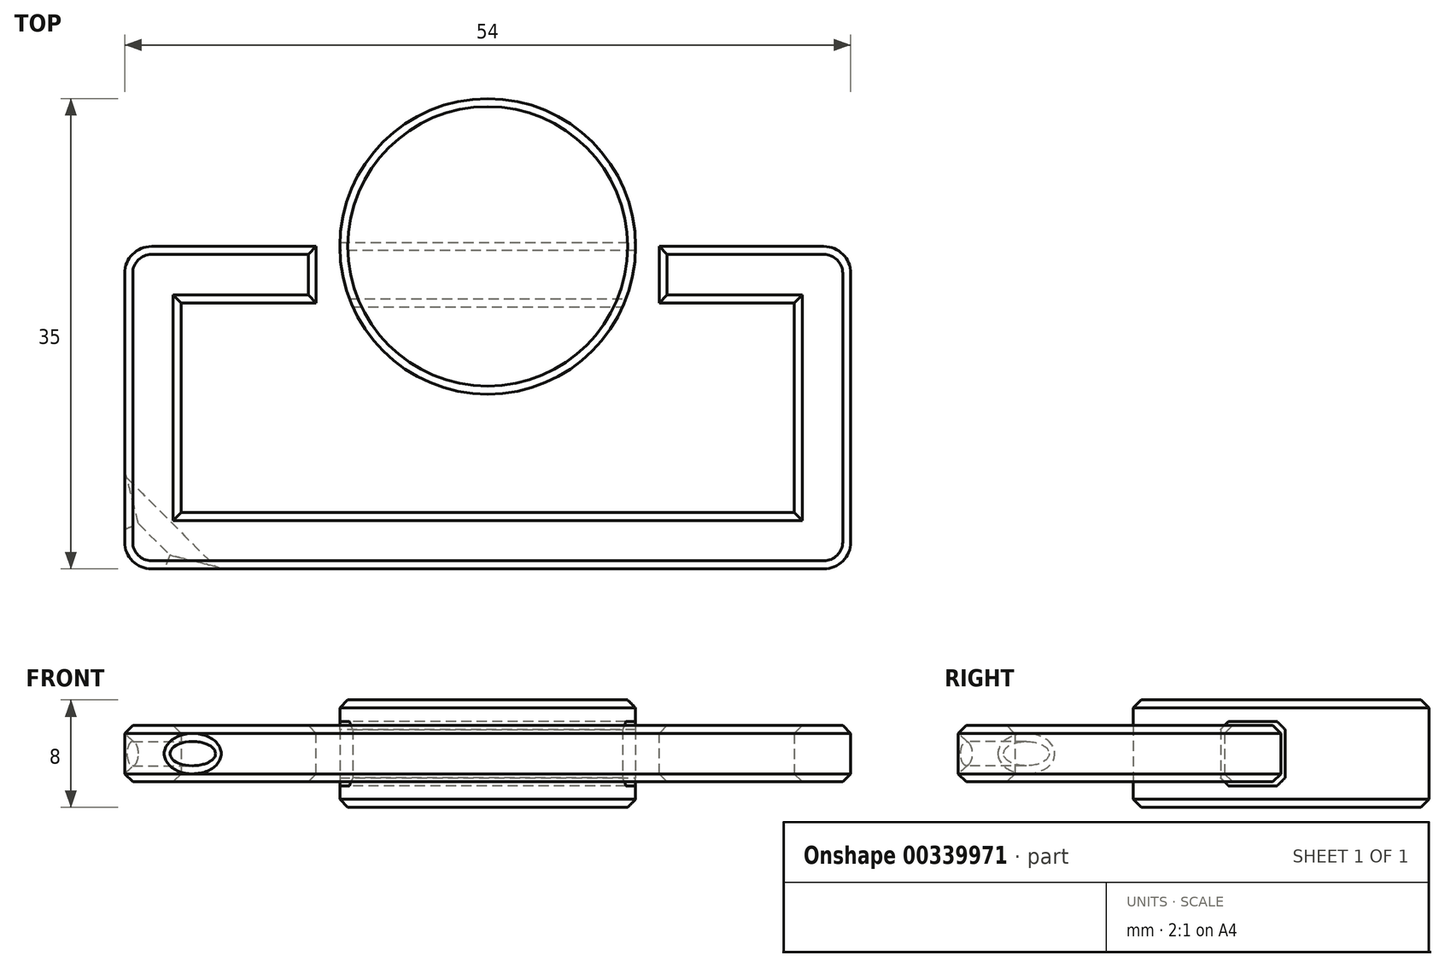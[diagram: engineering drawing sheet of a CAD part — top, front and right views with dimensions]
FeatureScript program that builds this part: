
annotation { "Feature Type Name" : "Feature", "Feature Type Description" : "" }
export const myFeature = defineFeature(function(context is Context, id is Id, definition is map)
    precondition{}
    {
        {
            var Q0;
            Q0=qCreatedBy(makeId("Top.planeOp"),FACE);
            var sketch = newSketch(context, id + "F0", { "sketchPlane" : qUnion([Q0])});
            skCircle(sketch, "E0", {"center": v(0, 0) * mm, "radius": 11 * mm});
            skSolve(sketch);
        }
        {
            var Q0;
            Q0 = qSketchRegion(id + "F0", true);
            extrude(context, id + "F1", {"entities" : qUnion([Q0]), "depth" : 4 * mm, "offsetDistance" : 25 * mm, "hasSecondDirection" : true, "secondDirectionOppositeDirection" : true, "secondDirectionDepth" : 4 * mm});
        }
        {
            var Q0;
            Q0=qCreatedBy(makeId("Top.planeOp"),FACE);
            var sketch = newSketch(context, id + "F2", { "sketchPlane" : qUnion([Q0])});
            skLineSegment(sketch, "E1.bottom", {"start": v(-27, 0) * mm, "end": v(27, 0) * mm});
            skLineSegment(sketch, "E1.top", {"start": v(-27, -24) * mm, "end": v(27, -24) * mm});
            skLineSegment(sketch, "E1.left", {"start": v(-27, 0) * mm, "end": v(-27, -24) * mm});
            skLineSegment(sketch, "E1.right", {"start": v(27, 0) * mm, "end": v(27, -24) * mm});
            skPoint(sketch, "E1.middle", {"position": v(0, -12) * mm});
            skLineSegment(sketch, "E2.0", {"start": v(-22.8, -4.2) * mm, "end": v(22.8, -4.2) * mm});
            skLineSegment(sketch, "E2.1", {"start": v(-22.8, -4.2) * mm, "end": v(-22.8, -19.8) * mm});
            skLineSegment(sketch, "E2.2", {"start": v(-22.8, -19.8) * mm, "end": v(22.8, -19.8) * mm});
            skLineSegment(sketch, "E2.3", {"start": v(22.8, -4.2) * mm, "end": v(22.8, -19.8) * mm});
            skSolve(sketch);
        }
        {
            var Q0;
            Q0 = qSketchRegion(id + "F2", true);
            extrude(context, id + "F3", {"entities" : qUnion([Q0]), "depth" : 2.1 * mm, "offsetDistance" : 25 * mm, "hasSecondDirection" : true, "secondDirectionOppositeDirection" : true, "secondDirectionDepth" : 2.1 * mm});
        }
        {
            var Q0;
            Q0=qCreatedBy(makeId("Top.planeOp"),FACE);
            var sketch = newSketch(context, id + "F4", { "sketchPlane" : qUnion([Q0])});
            skLineSegment(sketch, "E3.bottom", {"start": v(-12.75, 0.3) * mm, "end": v(12.75, 0.3) * mm});
            skLineSegment(sketch, "E3.top", {"start": v(-12.75, -4.5) * mm, "end": v(12.75, -4.5) * mm});
            skLineSegment(sketch, "E3.left", {"start": v(-12.75, 0.3) * mm, "end": v(-12.75, -4.5) * mm});
            skLineSegment(sketch, "E3.right", {"start": v(12.75, 0.3) * mm, "end": v(12.75, -4.5) * mm});
            skPoint(sketch, "E3.middle", {"position": v(0, -2.1) * mm});
            skSolve(sketch);
        }
        {
            var Q0;
            Q0 = qSketchRegion(id + "F4", true);
            extrude(context, id + "F5", {"entities" : qUnion([Q0]), "operationType" : NewBodyOperationType.REMOVE, "oppositeDirection" : true, "depth" : 2.4 * mm, "offsetDistance" : 25 * mm, "hasSecondDirection" : true, "secondDirectionOppositeDirection" : false, "secondDirectionDepth" : 2.4 * mm});
        }
        {
            var Q0;
            Q0=makeQuery(id+"F3.opExtrude","SWEPT_EDGE",EDGE,{"disambiguationData":[OSD([sQuery(id+"F2.wireOp",EDGE,"E1.bottom"),sQuery(id+"F2.wireOp",EDGE,"E1.left")])]});
            var Q1;
            Q1=makeQuery(id+"F3.opExtrude","SWEPT_EDGE",EDGE,{"disambiguationData":[OSD([sQuery(id+"F2.wireOp",EDGE,"E1.bottom"),sQuery(id+"F2.wireOp",EDGE,"E1.right")])]});
            var Q2;
            Q2=makeQuery(id+"F3.opExtrude","SWEPT_EDGE",EDGE,{"disambiguationData":[OSD([sQuery(id+"F2.wireOp",EDGE,"E1.top"),sQuery(id+"F2.wireOp",EDGE,"E1.right")])]});
            var Q3;
            Q3=makeQuery(id+"F3.opExtrude","SWEPT_EDGE",EDGE,{"disambiguationData":[OSD([sQuery(id+"F2.wireOp",EDGE,"E1.top"),sQuery(id+"F2.wireOp",EDGE,"E1.left")])]});
            fillet(context, id + "F6", {"entities" : qUnion([Q0, Q1, Q2, Q3]), "radius" : 2 * mm, "tangentPropagation" : true, "allowEdgeOverflow" : false});
        }
        {
            var Q0;
            Q0=makeQuery(id+"F3.opExtrude","CAP_FACE",FACE,{"disambiguationData":[OSD([sQuery(id+"F2.wireOp",EDGE,"E1.bottom"),sQuery(id+"F2.wireOp",EDGE,"E1.top"),sQuery(id+"F2.wireOp",EDGE,"E1.left"),sQuery(id+"F2.wireOp",EDGE,"E1.right"),sQuery(id+"F2.wireOp",EDGE,"E2.0"),sQuery(id+"F2.wireOp",EDGE,"E2.1"),sQuery(id+"F2.wireOp",EDGE,"E2.2"),sQuery(id+"F2.wireOp",EDGE,"E2.3")])],"isStart":false});
            var Q1;
            Q1=makeQuery(id+"F3.opExtrude","CAP_FACE",FACE,{"disambiguationData":[OSD([sQuery(id+"F2.wireOp",EDGE,"E1.bottom"),sQuery(id+"F2.wireOp",EDGE,"E1.top"),sQuery(id+"F2.wireOp",EDGE,"E1.left"),sQuery(id+"F2.wireOp",EDGE,"E1.right"),sQuery(id+"F2.wireOp",EDGE,"E2.0"),sQuery(id+"F2.wireOp",EDGE,"E2.1"),sQuery(id+"F2.wireOp",EDGE,"E2.2"),sQuery(id+"F2.wireOp",EDGE,"E2.3")])],"isStart":true});
            var Q2;
            Q2=makeQuery(id+"F1.opExtrude","CAP_FACE",FACE,{"disambiguationData":[OSD([sQuery(id+"F0.wireOp",EDGE,"E0")])],"isStart":false});
            var Q3;
            Q3=makeQuery(id+"F1.opExtrude","CAP_FACE",FACE,{"disambiguationData":[OSD([sQuery(id+"F0.wireOp",EDGE,"E0")])],"isStart":true});
            var Q4;
            Q4=makeQuery(id+"F5.boolean.opBoolean","COPY",EDGE,{"derivedFrom":makeQuery(id+"F5.opExtrude","CAP_EDGE",EDGE,{"disambiguationData":[OSD([sQuery(id+"F4.wireOp",EDGE,"E3.bottom")])],"isStart":false})});
            var Q5;
            Q5=makeQuery(id+"F5.boolean.opBoolean","COPY",EDGE,{"derivedFrom":makeQuery(id+"F5.opExtrude","CAP_EDGE",EDGE,{"disambiguationData":[OSD([sQuery(id+"F4.wireOp",EDGE,"E3.bottom")])],"isStart":true})});
            var Q6;
            Q6=makeQuery(id+"F5.boolean.opBoolean","COPY",EDGE,{"derivedFrom":makeQuery(id+"F5.opExtrude","CAP_EDGE",EDGE,{"disambiguationData":[OSD([sQuery(id+"F4.wireOp",EDGE,"E3.top")])],"isStart":true})});
            var Q7;
            Q7=makeQuery(id+"F5.boolean.opBoolean","COPY",EDGE,{"derivedFrom":makeQuery(id+"F5.opExtrude","CAP_EDGE",EDGE,{"disambiguationData":[OSD([sQuery(id+"F4.wireOp",EDGE,"E3.top")])],"isStart":false})});
            chamfer(context, id + "F7", {"entities" : qUnion([Q0, Q1, Q2, Q3, Q4, Q5, Q6, Q7]), "width" : 0.6 * mm, "tangentPropagation" : true});
        }
        {
            var Q0;
            Q0=makeQuery(id+"F3.opExtrude","CAP_FACE",FACE,{"disambiguationData":[OSD([sQuery(id+"F2.wireOp",EDGE,"E1.bottom"),sQuery(id+"F2.wireOp",EDGE,"E1.top"),sQuery(id+"F2.wireOp",EDGE,"E1.left"),sQuery(id+"F2.wireOp",EDGE,"E1.right"),sQuery(id+"F2.wireOp",EDGE,"E2.0"),sQuery(id+"F2.wireOp",EDGE,"E2.1"),sQuery(id+"F2.wireOp",EDGE,"E2.2"),sQuery(id+"F2.wireOp",EDGE,"E2.3")])],"isStart":false});
            var sketch = newSketch(context, id + "F8", { "sketchPlane" : qUnion([Q0])});
            skLineSegment(sketch, "E4", {"start": v(-23.2, -23.4) * mm, "end": v(-26.4, -20.2) * mm});
            skLineSegment(sketch, "E5", {"start": v(-26.4, -20.2) * mm, "end": v(-28.8, -17.8) * mm});
            skLineSegment(sketch, "E6", {"start": v(-28.8, -17.8) * mm, "end": v(-27.53, -16.53) * mm});
            skLineSegment(sketch, "E7", {"start": v(-27.53, -16.53) * mm, "end": v(-18.47, -25.6) * mm});
            skLineSegment(sketch, "E8", {"start": v(-23.2, -23.4) * mm, "end": v(-20.02, -26.6) * mm});
            skLineSegment(sketch, "E9", {"start": v(-20.02, -26.6) * mm, "end": v(-18.75, -25.32) * mm});
            skSolve(sketch);
        }
        {
            var Q0;
            Q0 = qSketchRegion(id + "F8", true);
            extrude(context, id + "F9", {"entities" : qUnion([Q0]), "operationType" : NewBodyOperationType.REMOVE, "oppositeDirection" : true, "depth" : (1.2 + 1.8) * mm, "offsetDistance" : 25 * mm, "hasSecondDirection" : true, "secondDirectionOppositeDirection" : true, "secondDirectionDepth" : 1.2 * mm});
        }
        {
            var Q0;
            Q0=makeQuery(id+"F9.boolean.opBoolean","COPY",EDGE,{"derivedFrom":makeQuery(id+"F9.opExtrude","CAP_EDGE",EDGE,{"disambiguationData":[OSD([sQuery(id+"F8.wireOp",EDGE,"E7")])],"isStart":false})});
            var Q1;
            Q1=makeQuery(id+"F9.boolean.opBoolean","COPY",EDGE,{"derivedFrom":makeQuery(id+"F9.opExtrude","CAP_EDGE",EDGE,{"disambiguationData":[OSD([sQuery(id+"F8.wireOp",EDGE,"E7")])],"isStart":true})});
            var Q2;
            Q2=makeQuery(id+"F9.boolean.opBoolean","COPY",EDGE,{"derivedFrom":makeQuery(id+"F9.opExtrude","CAP_EDGE",EDGE,{"disambiguationData":[OSD([sQuery(id+"F8.wireOp",EDGE,"E4"),sQuery(id+"F8.wireOp",EDGE,"E5"),sQuery(id+"F8.wireOp",EDGE,"E8")])],"isStart":true})});
            var Q3;
            Q3=makeQuery(id+"F9.boolean.opBoolean","COPY",EDGE,{"derivedFrom":makeQuery(id+"F9.opExtrude","CAP_EDGE",EDGE,{"disambiguationData":[OSD([sQuery(id+"F8.wireOp",EDGE,"E4"),sQuery(id+"F8.wireOp",EDGE,"E5"),sQuery(id+"F8.wireOp",EDGE,"E8")])],"isStart":false})});
            fillet(context, id + "F10", {"entities" : qUnion([Q0, Q1, Q2, Q3]), "radius" : 0.9 * mm, "tangentPropagation" : true, "allowEdgeOverflow" : false});
        }
        {
            var Q0;
            Q0=makeQuery(id+"F10.opFillet","BLEND_EDGE",EDGE,{"blendedFrom":[makeQuery(id+"F9.boolean.opBoolean","COPY",EDGE,{"derivedFrom":makeQuery(id+"F9.opExtrude","CAP_EDGE",EDGE,{"disambiguationData":[OSD([sQuery(id+"F8.wireOp",EDGE,"E4"),sQuery(id+"F8.wireOp",EDGE,"E5"),sQuery(id+"F8.wireOp",EDGE,"E8")])],"isStart":true})}),makeQuery(id+"F3.opExtrude","SWEPT_FACE",FACE,{"disambiguationData":[OSD([sQuery(id+"F2.wireOp",EDGE,"E1.top")])]})],"blendedInto":[makeQuery(id+"F3.opExtrude","SWEPT_FACE",FACE,{"disambiguationData":[OSD([sQuery(id+"F2.wireOp",EDGE,"E1.top")])]})]});
            var Q1;
            Q1=makeQuery(id+"F10.opFillet","BLEND_EDGE",EDGE,{"blendedFrom":[makeQuery(id+"F9.boolean.opBoolean","COPY",EDGE,{"derivedFrom":makeQuery(id+"F9.opExtrude","CAP_EDGE",EDGE,{"disambiguationData":[OSD([sQuery(id+"F8.wireOp",EDGE,"E4"),sQuery(id+"F8.wireOp",EDGE,"E5"),sQuery(id+"F8.wireOp",EDGE,"E8")])],"isStart":true})}),makeQuery(id+"F3.opExtrude","SWEPT_FACE",FACE,{"disambiguationData":[OSD([sQuery(id+"F2.wireOp",EDGE,"E1.left")])]})],"blendedInto":[makeQuery(id+"F3.opExtrude","SWEPT_FACE",FACE,{"disambiguationData":[OSD([sQuery(id+"F2.wireOp",EDGE,"E1.left")])]})]});
            chamfer(context, id + "F11", {"entities" : qUnion([Q0, Q1]), "width" : 0.6 * mm, "tangentPropagation" : true});
        }
    });
